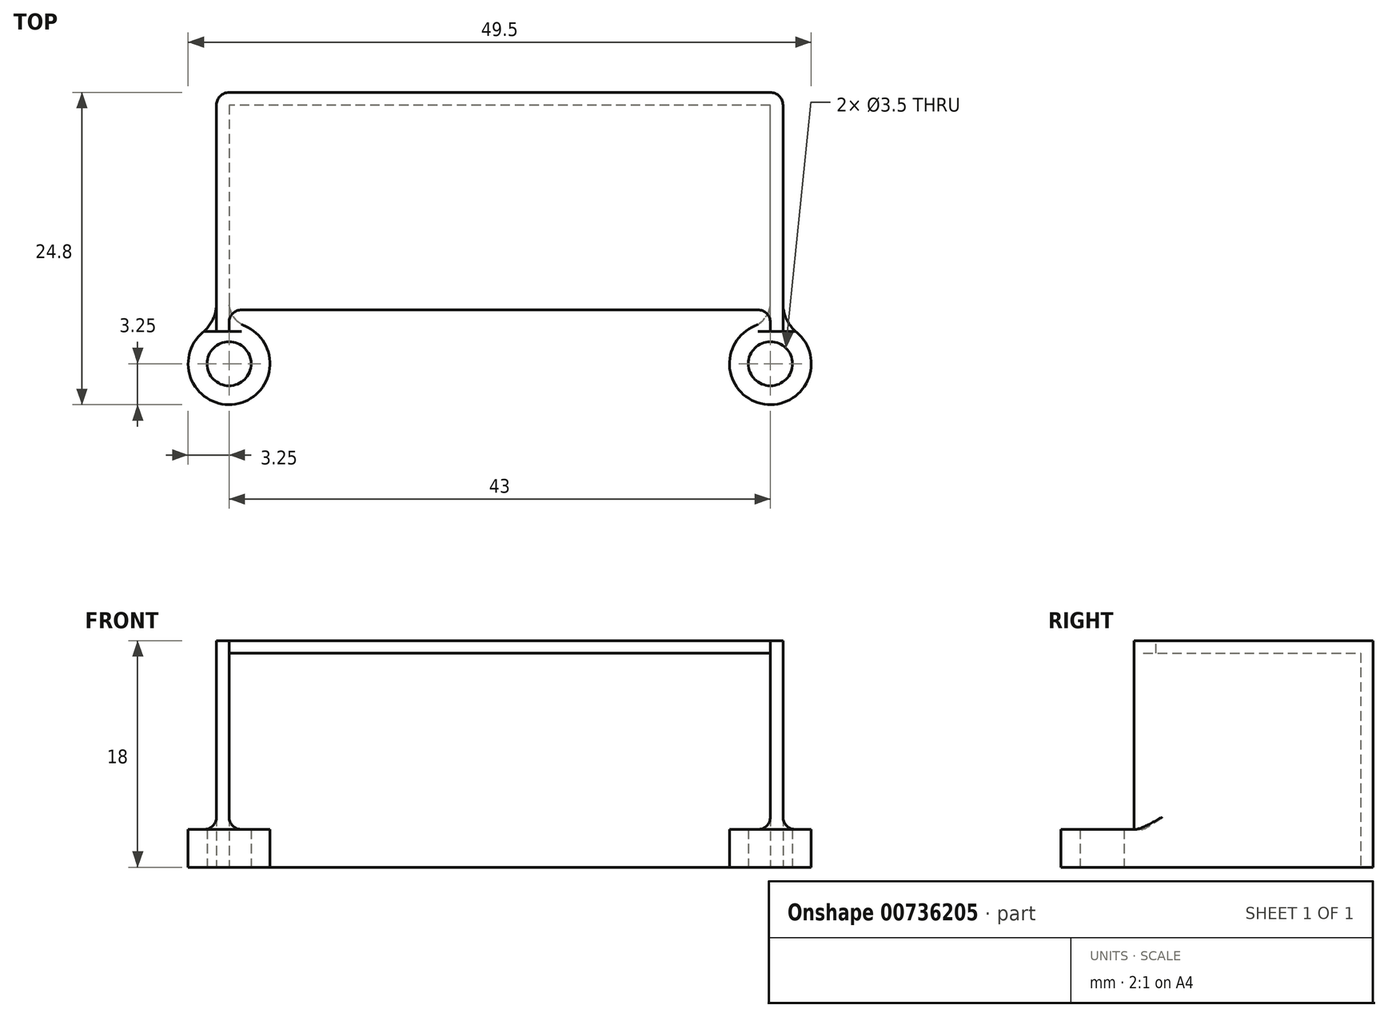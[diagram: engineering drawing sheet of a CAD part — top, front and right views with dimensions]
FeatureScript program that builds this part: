
annotation { "Feature Type Name" : "Feature", "Feature Type Description" : "" }
export const myFeature = defineFeature(function(context is Context, id is Id, definition is map)
    precondition{}
    {
        {
            var Q0;
            Q0=qCreatedBy(makeId("Top.planeOp"),FACE);
            var sketch = newSketch(context, id + "F0", { "sketchPlane" : qUnion([Q0])});
            skLineSegment(sketch, "E0", {"start": v(-22.5, 16) * mm, "end": v(22.5, 16) * mm});
            skLineSegment(sketch, "E1", {"start": v(22.5, 16) * mm, "end": v(22.5, -3) * mm});
            skLineSegment(sketch, "E2", {"start": v(22.5, -3) * mm, "end": v(21.5, -3) * mm});
            skLineSegment(sketch, "E3", {"start": v(21.5, -3) * mm, "end": v(21.5, 15) * mm});
            skLineSegment(sketch, "E4", {"start": v(21.5, 15) * mm, "end": v(-21.5, 15) * mm});
            skLineSegment(sketch, "E5", {"start": v(-21.5, 15) * mm, "end": v(-21.5, -3) * mm});
            skLineSegment(sketch, "E6", {"start": v(-21.5, -3) * mm, "end": v(-22.5, -3) * mm});
            skLineSegment(sketch, "E7", {"start": v(-22.5, -3) * mm, "end": v(-22.5, 16) * mm});
            skSolve(sketch);
        }
        {
            var Q0;
            Q0 = qSketchRegion(id + "F0", true);
            extrude(context, id + "F1", {"entities" : qUnion([Q0]), "depth" : 18 * mm, "offsetDistance" : 25 * mm});
        }
        {
            var Q0;
            Q0=qCreatedBy(makeId("Top.planeOp"),FACE);
            var sketch = newSketch(context, id + "F2", { "sketchPlane" : qUnion([Q0])});
            skCircle(sketch, "E8", {"center": v(-21.5, -5.55) * mm, "radius": 3.25 * mm});
            skCircle(sketch, "E9", {"center": v(21.5, -5.55) * mm, "radius": 3.25 * mm});
            skSolve(sketch);
        }
        {
            var Q0;
            Q0 = qSketchRegion(id + "F2", true);
            extrude(context, id + "F3", {"entities" : qUnion([Q0]), "operationType" : NewBodyOperationType.ADD, "depth" : 3 * mm, "offsetDistance" : 25 * mm});
        }
        {
            var Q0;
            Q0=makeQuery(id+"F1.opExtrude","CAP_FACE",FACE,{"disambiguationData":[OSD([sQuery(id+"F0.wireOp",EDGE,"E0"),sQuery(id+"F0.wireOp",EDGE,"E1"),sQuery(id+"F0.wireOp",EDGE,"E2"),sQuery(id+"F0.wireOp",EDGE,"E3"),sQuery(id+"F0.wireOp",EDGE,"E4"),sQuery(id+"F0.wireOp",EDGE,"E5"),sQuery(id+"F0.wireOp",EDGE,"E6"),sQuery(id+"F0.wireOp",EDGE,"E7")])],"isStart":false});
            cPlane(context, id + "F4", {"entities" : qUnion([Q0]), "cplaneType" : CPlaneType.OFFSET, "offset" : 0 * mm, "width" : 150 * mm, "height" : 150 * mm});
        }
        {
            var Q0;
            Q0=qCreatedBy(id+"F4.planeOp",FACE);
            var sketch = newSketch(context, id + "F5", { "sketchPlane" : qUnion([Q0])});
            skLineSegment(sketch, "E10.bottom", {"start": v(-22.5, -1.27) * mm, "end": v(22.5, -1.27) * mm});
            skLineSegment(sketch, "E10.top", {"start": v(-22.5, 16) * mm, "end": v(22.5, 16) * mm});
            skLineSegment(sketch, "E10.left", {"start": v(-22.5, -1.27) * mm, "end": v(-22.5, 16) * mm});
            skLineSegment(sketch, "E10.right", {"start": v(22.5, -1.27) * mm, "end": v(22.5, 16) * mm});
            skSolve(sketch);
        }
        {
            var Q0;
            Q0 = qSketchRegion(id + "F5", true);
            extrude(context, id + "F6", {"entities" : qUnion([Q0]), "operationType" : NewBodyOperationType.ADD, "oppositeDirection" : true, "depth" : 1 * mm, "offsetDistance" : 25 * mm});
        }
        {
            var Q0;
            Q0=qCreatedBy(makeId("Top.planeOp"),FACE);
            var sketch = newSketch(context, id + "F7", { "sketchPlane" : qUnion([Q0])});
            skCircle(sketch, "E11", {"center": v(21.5, -5.55) * mm, "radius": 1.75 * mm});
            skCircle(sketch, "E12", {"center": v(-21.5, -5.55) * mm, "radius": 1.75 * mm});
            skSolve(sketch);
        }
        {
            var Q0;
            Q0 = qSketchRegion(id + "F7", true);
            extrude(context, id + "F8", {"entities" : qUnion([Q0]), "operationType" : NewBodyOperationType.REMOVE, "depth" : 25 * mm, "offsetDistance" : 25 * mm});
        }
        {
            var Q0;
            Q0=makeQuery(id+"F3.boolean.opBoolean","INTERSECT",EDGE,{"derivedFrom":[makeQuery(id+"F1.opExtrude","SWEPT_FACE",FACE,{"disambiguationData":[OSD([sQuery(id+"F0.wireOp",EDGE,"E1")])]}),makeQuery(id+"F3.opExtrude","SWEPT_FACE",FACE,{"disambiguationData":[OSD([sQuery(id+"F2.wireOp",EDGE,"E9")])]})]});
            fillet(context, id + "F9", {"entities" : qUnion([Q0]), "radius" : 3 * mm, "tangentPropagation" : true, "allowEdgeOverflow" : false});
        }
        {
            var Q0;
            Q0=makeQuery(id+"F3.boolean.opBoolean","INTERSECT",EDGE,{"derivedFrom":[makeQuery(id+"F1.opExtrude","SWEPT_FACE",FACE,{"disambiguationData":[OSD([sQuery(id+"F0.wireOp",EDGE,"E1")])]}),makeQuery(id+"F3.opExtrude","CAP_FACE",FACE,{"disambiguationData":[OSD([sQuery(id+"F2.wireOp",EDGE,"E9")])],"isStart":false})]});
            fillet(context, id + "F10", {"entities" : qUnion([Q0]), "radius" : 1 * mm, "tangentPropagation" : true, "allowEdgeOverflow" : false});
        }
        {
            var Q0;
            Q0=makeQuery(id+"F3.boolean.opBoolean","INTERSECT",EDGE,{"derivedFrom":[makeQuery(id+"F1.opExtrude","SWEPT_FACE",FACE,{"disambiguationData":[OSD([sQuery(id+"F0.wireOp",EDGE,"E7")])]}),makeQuery(id+"F3.opExtrude","SWEPT_FACE",FACE,{"disambiguationData":[OSD([sQuery(id+"F2.wireOp",EDGE,"E8")])]})]});
            fillet(context, id + "F11", {"entities" : qUnion([Q0]), "radius" : 3 * mm, "tangentPropagation" : true, "allowEdgeOverflow" : false});
        }
        {
            var Q0;
            Q0=makeQuery(id+"F3.boolean.opBoolean","INTERSECT",EDGE,{"derivedFrom":[makeQuery(id+"F1.opExtrude","SWEPT_FACE",FACE,{"disambiguationData":[OSD([sQuery(id+"F0.wireOp",EDGE,"E7")])]}),makeQuery(id+"F3.opExtrude","CAP_FACE",FACE,{"disambiguationData":[OSD([sQuery(id+"F2.wireOp",EDGE,"E8")])],"isStart":false})]});
            fillet(context, id + "F12", {"entities" : qUnion([Q0]), "radius" : (1) * mm, "tangentPropagation" : true, "allowEdgeOverflow" : false});
        }
        {
            var Q0;
            Q0=makeQuery(id+"F1.opExtrude","SWEPT_EDGE",EDGE,{"disambiguationData":[OSD([sQuery(id+"F0.wireOp",EDGE,"E0"),sQuery(id+"F0.wireOp",EDGE,"E7")])]});
            fillet(context, id + "F13", {"entities" : qUnion([Q0]), "radius" : 1 * mm, "tangentPropagation" : true, "allowEdgeOverflow" : false});
        }
        {
            var Q0;
            Q0=makeQuery(id+"F1.opExtrude","SWEPT_EDGE",EDGE,{"disambiguationData":[OSD([sQuery(id+"F0.wireOp",EDGE,"E0"),sQuery(id+"F0.wireOp",EDGE,"E1")])]});
            fillet(context, id + "F14", {"entities" : qUnion([Q0]), "radius" : 1 * mm, "tangentPropagation" : true, "allowEdgeOverflow" : false});
        }
        {
            var Q0;
            Q0=makeQuery(id+"F6.boolean.opBoolean","INTERSECT",EDGE,{"derivedFrom":[makeQuery(id+"F1.opExtrude","SWEPT_FACE",FACE,{"disambiguationData":[OSD([sQuery(id+"F0.wireOp",EDGE,"E5")])]}),makeQuery(id+"F6.opExtrude","SWEPT_FACE",FACE,{"disambiguationData":[OSD([sQuery(id+"F5.wireOp",EDGE,"E10.bottom")])]})]});
            fillet(context, id + "F15", {"entities" : qUnion([Q0]), "radius" : 1 * mm, "tangentPropagation" : true, "allowEdgeOverflow" : false});
        }
        {
            var Q0;
            Q0=makeQuery(id+"F6.boolean.opBoolean","INTERSECT",EDGE,{"derivedFrom":[makeQuery(id+"F1.opExtrude","SWEPT_FACE",FACE,{"disambiguationData":[OSD([sQuery(id+"F0.wireOp",EDGE,"E3")])]}),makeQuery(id+"F6.opExtrude","SWEPT_FACE",FACE,{"disambiguationData":[OSD([sQuery(id+"F5.wireOp",EDGE,"E10.bottom")])]})]});
            fillet(context, id + "F16", {"entities" : qUnion([Q0]), "radius" : 1 * mm, "tangentPropagation" : true, "allowEdgeOverflow" : false});
        }
        {
            var Q0;
            Q0=makeQuery(id+"F3.boolean.opBoolean","INTERSECT",EDGE,{"derivedFrom":[makeQuery(id+"F1.opExtrude","SWEPT_FACE",FACE,{"disambiguationData":[OSD([sQuery(id+"F0.wireOp",EDGE,"E5")])]}),makeQuery(id+"F3.opExtrude","SWEPT_FACE",FACE,{"disambiguationData":[OSD([sQuery(id+"F2.wireOp",EDGE,"E8")])]})]});
            fillet(context, id + "F17", {"entities" : qUnion([Q0]), "radius" : 2 * mm, "tangentPropagation" : true, "allowEdgeOverflow" : false});
        }
        {
            var Q0;
            Q0=makeQuery(id+"F3.boolean.opBoolean","INTERSECT",EDGE,{"derivedFrom":[makeQuery(id+"F1.opExtrude","SWEPT_FACE",FACE,{"disambiguationData":[OSD([sQuery(id+"F0.wireOp",EDGE,"E5")])]}),makeQuery(id+"F3.opExtrude","CAP_FACE",FACE,{"disambiguationData":[OSD([sQuery(id+"F2.wireOp",EDGE,"E8")])],"isStart":false})]});
            fillet(context, id + "F18", {"entities" : qUnion([Q0]), "radius" : 1 * mm, "tangentPropagation" : true, "allowEdgeOverflow" : false});
        }
        {
            var Q0;
            Q0=makeQuery(id+"F3.boolean.opBoolean","INTERSECT",EDGE,{"derivedFrom":[makeQuery(id+"F1.opExtrude","SWEPT_FACE",FACE,{"disambiguationData":[OSD([sQuery(id+"F0.wireOp",EDGE,"E3")])]}),makeQuery(id+"F3.opExtrude","SWEPT_FACE",FACE,{"disambiguationData":[OSD([sQuery(id+"F2.wireOp",EDGE,"E9")])]})]});
            fillet(context, id + "F19", {"entities" : qUnion([Q0]), "radius" : 2 * mm, "tangentPropagation" : true, "allowEdgeOverflow" : false});
        }
        {
            var Q0;
            Q0=makeQuery(id+"F3.boolean.opBoolean","INTERSECT",EDGE,{"derivedFrom":[makeQuery(id+"F1.opExtrude","SWEPT_FACE",FACE,{"disambiguationData":[OSD([sQuery(id+"F0.wireOp",EDGE,"E3")])]}),makeQuery(id+"F3.opExtrude","CAP_FACE",FACE,{"disambiguationData":[OSD([sQuery(id+"F2.wireOp",EDGE,"E9")])],"isStart":false})]});
            fillet(context, id + "F20", {"entities" : qUnion([Q0]), "radius" : 1 * mm, "tangentPropagation" : true, "allowEdgeOverflow" : false});
        }
    });
